# Revit family: RA-C_DN15-20_RFA_3
name_source: partatom
category: Pipe Accessories
units: mm (PartAtom-declared; Revit-internal decimal feet)

## family parameters
Always vertical = Yes
Cut with Voids When Loaded = No
OmniClass Number = 23.65.55.14.17
OmniClass Title = Adjusting/Controlling Valves for Liquid Services
Part Type = Valve - Breaks Into
Round Connector Dimension = Use Diameter
Shared = No
Work Plane-Based = No

## types (2) — shared parameters
Connection = External Thread
D_B2 = 23 mm  [stored 0.0754593 ft]
D_B3 = 17 mm
D_B4 = 19 mm  [stored 0.062336 ft]
Description = Motorized Control Valve
IfcExportAs = IfcValveType
IfcExportType = RA-C
LOD 200 = No
LOD 350 = Yes
Manufacturer = Danfoss
Max Differential Pressure = 0.6 bar
Max Medium Temperature = 120 °C
Max Operating Pressure = 10 bar
Min Medium Temperature = -10 °C
URL = https://store.danfoss.com
Valve Body Material = Danfoss Brass (Nickel plated)

## per-type parameters (varying)
- RA-C_DN20_013G3096: D=20 mm  [stored 0.0656168 ft]; DN15=No; DN20=Yes; DN20_350=Yes; D_B1=43 mm  [stored 0.141076 ft]; D_Thread=34 mm; H0=63 mm  [stored 0.206693 ft]; H1=31 mm; H2=5 mm  [stored 0.0164042 ft]; H3=18 mm  [stored 0.0590551 ft]; H4=16 mm  [stored 0.0524934 ft]; H5=6 mm  [stored 0.019685 ft]; H6=-9 mm; H7=22 mm  [stored 0.0721785 ft]; H_Arc1=7 mm  [stored 0.0229659 ft]; H_Arc2=3 mm  [stored 0.00984252 ft]; Kvs=3.3 m³/h; L=77 mm  [stored 0.252625 ft]; L1=8 mm  [stored 0.0262467 ft]; L2=2 mm  [stored 0.00656168 ft]; L3=43 mm  [stored 0.141076 ft]; Model=013G3096; Model Type=RA-C_DN20; R_B1=18 mm  [stored 0.0590551 ft]; R_V1=31 mm; W=43 mm  [stored 0.141076 ft]; Weight=0.42 kg
- RA-C_DN15_013G3094: D=15 mm  [stored 0.0492126 ft]; DN15=Yes; DN20=No; DN20_350=No; D_B1=29 mm  [stored 0.0951444 ft]; D_Thread=27 mm; H0=51 mm; H1=20 mm  [stored 0.0656168 ft]; H2=11 mm  [stored 0.0360892 ft]; H3=6 mm  [stored 0.019685 ft]; H4=17 mm; H5=7 mm  [stored 0.0229659 ft]; H6=-6 mm; H7=14 mm  [stored 0.0459318 ft]; H_Arc1=0 mm  [stored 0 ft]; H_Arc2=0 mm  [stored 0 ft]; Kvs=1.2 m³/h; L=66 mm  [stored 0.216535 ft]; L1=7 mm  [stored 0.0229659 ft]; L2=3 mm  [stored 0.00984252 ft]; L3=10 mm  [stored 0.0328084 ft]; Model=013G3094; Model Type=RA-C_DN15; R_B1=10 mm  [stored 0.0328084 ft]; R_V1=23 mm  [stored 0.0754593 ft]; W=29 mm  [stored 0.0951444 ft]; Weight=0.22 kg

note: [stored X ft] marks values corroborated as IEEE doubles in the binary element streams (Revit-internal decimal feet)

## geometry (parser evidence)
native form markers: Sweep x4
no freeform markers — native parametric forms only
